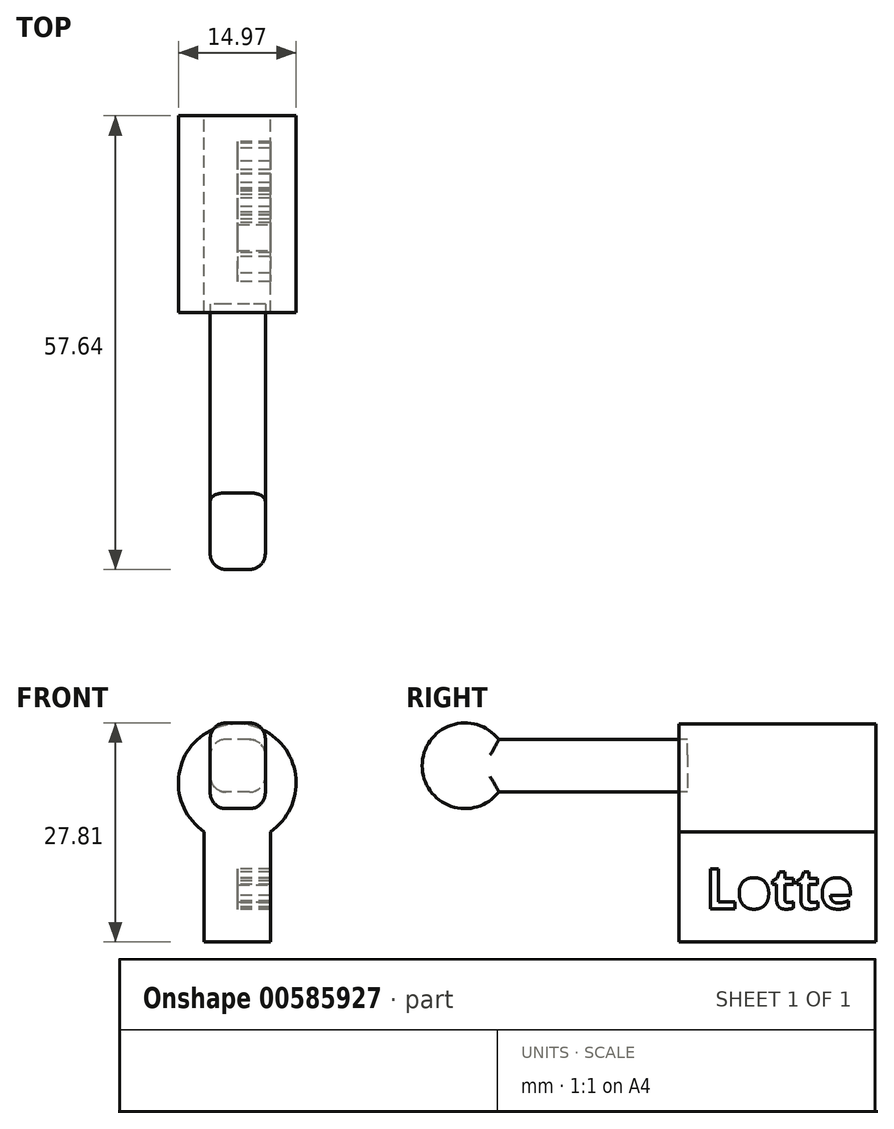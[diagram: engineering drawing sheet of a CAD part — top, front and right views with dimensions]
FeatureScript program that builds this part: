
annotation { "Feature Type Name" : "Feature", "Feature Type Description" : "" }
export const myFeature = defineFeature(function(context is Context, id is Id, definition is map)
    precondition{}
    {
        {
            var Q0;
            Q0=qCreatedBy(makeId("Front.planeOp"),FACE);
            var sketch = newSketch(context, id + "F0", { "sketchPlane" : qUnion([Q0])});
            skCircle(sketch, "E0", {"center": v(-0.06, 10.88) * mm, "radius": 7.48 * mm});
            skLineSegment(sketch, "E1.bottom", {"start": v(4.14, -9.31) * mm, "end": v(-4.26, -9.31) * mm});
            skLineSegment(sketch, "E1.top", {"start": v(4.14, 4.69) * mm, "end": v(-4.26, 4.69) * mm});
            skLineSegment(sketch, "E1.left", {"start": v(4.14, -9.31) * mm, "end": v(4.14, 4.69) * mm});
            skLineSegment(sketch, "E1.right", {"start": v(-4.26, -9.31) * mm, "end": v(-4.26, 4.69) * mm});
            skSolve(sketch);
        }
        {
            var Q0;
            Q0 = qSketchRegion(id + "F0", true);
            extrude(context, id + "F1", {"entities" : qUnion([Q0]), "depth" : 25 * mm, "offsetDistance" : 25 * mm});
        }
        {
            var Q0;
            Q0=qCreatedBy(makeId("Right.planeOp"),FACE);
            var sketch = newSketch(context, id + "F2", { "sketchPlane" : qUnion([Q0])});
            skText(sketch, "E2", { "text": "Lotte\n", "fontName": "OpenSans-Bold.ttf"});
            const initialGuessF2  = {"E2": [-0.02168, -0.0051, 1, 0, 0.0051]};
            skSetInitialGuess(sketch, initialGuessF2);
            skSolve(sketch);
        }
        {
            var Q0;
            Q0 = qSketchRegion(id + "F2", true);
            var Q1;
            Q1=makeQuery(id+"F2.imprint","IMPRINT",FACE,{"disambiguationData":[TD([[makeQuery(id+"F2.imprint","IMPRINT",EDGE,{"derivedFrom":sQuery(id+"F2.wireOp",EDGE,"E2.sketch_text.stroke-6")}),1.0]])]});
            var Q2;
            Q2=makeQuery(id+"F2.imprint","IMPRINT",FACE,{"disambiguationData":[TD([[makeQuery(id+"F2.imprint","IMPRINT",EDGE,{"derivedFrom":sQuery(id+"F2.wireOp",EDGE,"E2.sketch_text.stroke-42")}),-1.0]])]});
            var Q3;
            Q3=makeQuery(id+"F2.imprint","IMPRINT",FACE,{"disambiguationData":[TD([[makeQuery(id+"F2.imprint","IMPRINT",EDGE,{"derivedFrom":sQuery(id+"F2.wireOp",EDGE,"E2.sketch_text.stroke-60")}),1.0]])]});
            var Q4;
            Q4=makeQuery(id+"F2.imprint","IMPRINT",FACE,{"disambiguationData":[TD([[makeQuery(id+"F2.imprint","IMPRINT",EDGE,{"derivedFrom":sQuery(id+"F2.wireOp",EDGE,"E2.sketch_text.stroke-60")}),-1.0]])]});
            var Q5;
            Q5 = qConstructionFilter(qBodyType(qCreatedBy(id + "F2" ,EDGE), BodyType.WIRE), ConstructionObject.NO);
            extrude(context, id + "F3", {"entities" : qUnion([Q0, Q1, Q2, Q3, Q4]), "operationType" : NewBodyOperationType.REMOVE, "surfaceEntities" : qUnion([Q5]), "depth" : 10 * mm, "offsetDistance" : 25 * mm});
        }
        {
            var Q0;
            Q0=qCreatedBy(makeId("Right.planeOp"),FACE);
            var sketch = newSketch(context, id + "F4", { "sketchPlane" : qUnion([Q0])});
            skLineSegment(sketch, "E3.bottom", {"start": v(-23.93, 16.4) * mm, "end": v(-47.93, 16.4) * mm});
            skLineSegment(sketch, "E3.top", {"start": v(-23.93, 9.72) * mm, "end": v(-47.93, 9.72) * mm});
            skLineSegment(sketch, "E3.left", {"start": v(-23.93, 16.4) * mm, "end": v(-23.93, 9.72) * mm});
            skLineSegment(sketch, "E3.right", {"start": v(-47.93, 16.4) * mm, "end": v(-47.93, 9.72) * mm});
            skCircle(sketch, "E4", {"center": v(-52.2, 13.06) * mm, "radius": 5.44 * mm});
            skPoint(sketch, "E4.centerSnap0", {"position": v(-47.93, 13.06) * mm});
            skSolve(sketch);
        }
        {
            var Q0;
            {var subQ0=sQuery(id+"F4.wireOp",EDGE,"E3.right");Q0=makeQuery(id+"F4.imprint","IMPRINT",FACE,{"disambiguationData":[TD([[makeQuery(id+"F4.imprint","IMPRINT",EDGE,{"derivedFrom":subQ0}),-1.0]])]});}
            var Q1;
            {var subQ0=sQuery(id+"F4.wireOp",EDGE,"E3.left");Q1=makeQuery(id+"F4.imprint","IMPRINT",FACE,{"disambiguationData":[TD([[makeQuery(id+"F4.imprint","IMPRINT",EDGE,{"derivedFrom":subQ0}),-1.0]])]});}
            var Q2;
            {var subQ0=sQuery(id+"F4.wireOp",EDGE,"E3.right");Q2=makeQuery(id+"F4.imprint","IMPRINT",FACE,{"disambiguationData":[TD([[makeQuery(id+"F4.imprint","IMPRINT",EDGE,{"derivedFrom":subQ0}),1.0]])]});}
            extrude(context, id + "F5", {"entities" : qUnion([Q0, Q1, Q2]), "endBound" : BoundingType.SYMMETRIC, "depth" : 7 * mm, "offsetDistance" : 25 * mm});
        }
        {
            var Q0;
            Q0=makeQuery(id+"F5.opExtrude","CAP_EDGE",EDGE,{"disambiguationData":[OSD([sQuery(id+"F4.wireOp",EDGE,"E3.bottom")])],"isStart":true});
            var Q1;
            Q1=makeQuery(id+"F5.opExtrude","CAP_EDGE",EDGE,{"disambiguationData":[OSD([sQuery(id+"F4.wireOp",EDGE,"E3.top")])],"isStart":true});
            var Q2;
            Q2=makeQuery(id+"F5.opExtrude","CAP_EDGE",EDGE,{"disambiguationData":[OSD([sQuery(id+"F4.wireOp",EDGE,"E3.bottom")])],"isStart":false});
            var Q3;
            Q3=makeQuery(id+"F5.opExtrude","CAP_EDGE",EDGE,{"disambiguationData":[OSD([sQuery(id+"F4.wireOp",EDGE,"E3.top")])],"isStart":false});
            var Q4;
            Q4=makeQuery(id+"F5.opExtrude","CAP_EDGE",EDGE,{"disambiguationData":[OSD([sQuery(id+"F4.wireOp",EDGE,"E4")])],"isStart":false});
            var Q5;
            Q5=makeQuery(id+"F5.opExtrude","CAP_EDGE",EDGE,{"disambiguationData":[OSD([sQuery(id+"F4.wireOp",EDGE,"E4")])],"isStart":true});
            fillet(context, id + "F6", {"entities" : qUnion([Q0, Q1, Q2, Q3, Q4, Q5]), "radius" : 2 * mm, "allowEdgeOverflow" : false});
        }
    });
